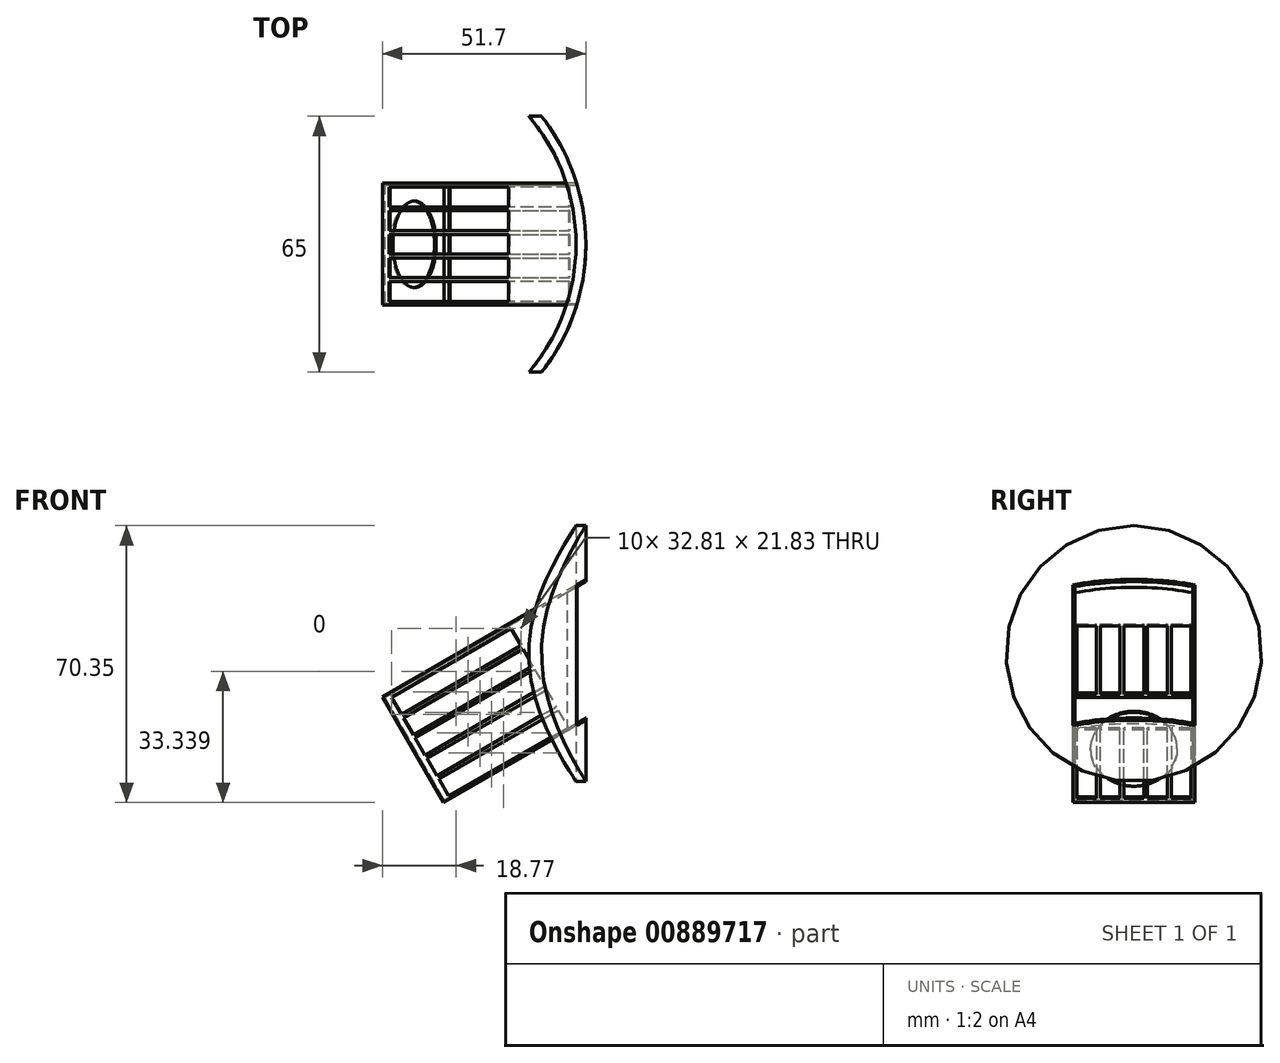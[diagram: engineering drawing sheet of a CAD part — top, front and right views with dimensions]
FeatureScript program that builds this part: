
annotation { "Feature Type Name" : "Feature", "Feature Type Description" : "" }
export const myFeature = defineFeature(function(context is Context, id is Id, definition is map)
    precondition{}
    {
        {
            var Q0;
            Q0=qCreatedBy(makeId("Top.planeOp"),FACE);
            var sketch = newSketch(context, id + "F0", { "sketchPlane" : qUnion([Q0])});
            skCircle(sketch, "E0", {"center": v(0, 0) * mm, "radius": 52.5 * mm});
            skCircle(sketch, "E1", {"center": v(0, 0) * mm, "radius": 50 * mm});
            skSolve(sketch);
        }
        {
            var Q0;
            Q0=makeQuery(id+"F0.imprint","IMPRINT",FACE,{"disambiguationData":[TD([[makeQuery(id+"F0.imprint","IMPRINT",EDGE,{"derivedFrom":sQuery(id+"F0.wireOp",EDGE,"E0")}),1.0]])]});
            var Q1;
            Q1=sQuery(id+"F0.wireOp",EDGE,"E1");
            var Q2;
            Q2=sQuery(id+"F0.wireOp",EDGE,"E0");
            extrude(context, id + "F1", {"entities" : qUnion([Q0]), "surfaceEntities" : qUnion([Q1, Q2]), "endBound" : BoundingType.SYMMETRIC, "depth" : 100 * mm, "offsetDistance" : 25 * mm});
        }
        {
            var Q0;
            Q0=qCreatedBy(makeId("Right.planeOp"),FACE);
            var sketch = newSketch(context, id + "F2", { "sketchPlane" : qUnion([Q0])});
            skCircle(sketch, "E2", {"center": v(0, 0) * mm, "radius": 32.5 * mm});
            skSolve(sketch);
        }
        {
            var Q0;
            Q0=makeQuery(id+"F2.imprint","IMPRINT",FACE,{"disambiguationData":[TD([[makeQuery(id+"F2.imprint","IMPRINT",EDGE,{"derivedFrom":sQuery(id+"F2.wireOp",EDGE,"E2")}),1.0]])]});
            var Q1;
            Q1=sQuery(id+"F2.wireOp",EDGE,"E2");
            extrude(context, id + "F3", {"entities" : qUnion([Q0]), "surfaceEntities" : qUnion([Q1]), "depth" : 60 * mm, "offsetDistance" : 25 * mm});
        }
        {
            var Q0;
            Q0=qCreatedBy(makeId("Right.planeOp"),FACE);
            var sketch = newSketch(context, id + "F4", { "sketchPlane" : qUnion([Q0])});
            skLineSegment(sketch, "E3.bottom", {"start": v(15.5, -15.5) * mm, "end": v(-15.5, -15.5) * mm});
            skLineSegment(sketch, "E3.top", {"start": v(15.5, 15.5) * mm, "end": v(-15.5, 15.5) * mm});
            skLineSegment(sketch, "E3.left", {"start": v(15.5, -15.5) * mm, "end": v(15.5, 15.5) * mm});
            skLineSegment(sketch, "E3.right", {"start": v(-15.5, -15.5) * mm, "end": v(-15.5, 15.5) * mm});
            skPoint(sketch, "E3.middle", {"position": v(0, 0) * mm});
            skSolve(sketch);
        }
        {
            var Q0;
            Q0=makeQuery(id+"F3.opExtrude","SWEPT_BODY",BODY,{"disambiguationData":[OSD([sQuery(id+"F2.wireOp",EDGE,"E2")])]});
            var Q1;
            Q1=makeQuery(id+"F1.opExtrude","SWEPT_BODY",BODY,{"disambiguationData":[OSD([sQuery(id+"F0.wireOp",EDGE,"E0"),sQuery(id+"F0.wireOp",EDGE,"E1")])]});
            booleanBodies(context, id + "F5", {"operationType" : BooleanOperationType.INTERSECTION, "tools" : qUnion([Q0, Q1])});
        }
        {
            var Q0;
            Q0 = qSketchRegion(id + "F4", true);
            extrude(context, id + "F6", {"entities" : qUnion([Q0]), "depth" : 60 * mm, "offsetDistance" : 25 * mm});
        }
        {
            var Q0;
            Q0=makeQuery(id+"F6.opExtrude","CAP_FACE",FACE,{"disambiguationData":[OSD([sQuery(id+"F4.wireOp",EDGE,"E3.bottom"),sQuery(id+"F4.wireOp",EDGE,"E3.top"),sQuery(id+"F4.wireOp",EDGE,"E3.left"),sQuery(id+"F4.wireOp",EDGE,"E3.right")])],"isStart":false});
            var sketch = newSketch(context, id + "F7", { "sketchPlane" : qUnion([Q0])});
            skLineSegment(sketch, "E4.bottom", {"start": v(-15, -15) * mm, "end": v(15, -15) * mm});
            skLineSegment(sketch, "E4.top", {"start": v(-15, 15) * mm, "end": v(15, 15) * mm});
            skLineSegment(sketch, "E4.left", {"start": v(-15, -15) * mm, "end": v(-15, 15) * mm});
            skLineSegment(sketch, "E4.right", {"start": v(15, -15) * mm, "end": v(15, 15) * mm});
            skPoint(sketch, "E4.middle", {"position": v(0, 0) * mm});
            skSolve(sketch);
        }
        {
            var Q0;
            Q0=makeQuery(id+"F7.imprint","IMPRINT",FACE,{"disambiguationData":[TD([[makeQuery(id+"F7.imprint","IMPRINT",EDGE,{"derivedFrom":sQuery(id+"F7.wireOp",EDGE,"E4.bottom")}),1.0]])]});
            extrude(context, id + "F8", {"entities" : qUnion([Q0]), "operationType" : NewBodyOperationType.REMOVE, "oppositeDirection" : true, "depth" : 59.5 * mm, "offsetDistance" : 25 * mm});
        }
        {
            var Q0;
            Q0=makeQuery(id+"F6.opExtrude","SWEPT_FACE",FACE,{"disambiguationData":[OSD([sQuery(id+"F4.wireOp",EDGE,"E3.top")])]});
            var sketch = newSketch(context, id + "F9", { "sketchPlane" : qUnion([Q0])});
            skLineSegment(sketch, "E5.bottom", {"start": v(2, -14.5) * mm, "end": v(37, -14.5) * mm});
            skLineSegment(sketch, "E5.top", {"start": v(2, -9.5) * mm, "end": v(37, -9.5) * mm});
            skLineSegment(sketch, "E5.left", {"start": v(2, -14.5) * mm, "end": v(2, -9.5) * mm});
            skLineSegment(sketch, "E6.bottom", {"start": v(37, -8.5) * mm, "end": v(2, -8.5) * mm});
            skLineSegment(sketch, "E6.top", {"start": v(37, -3.5) * mm, "end": v(2, -3.5) * mm});
            skLineSegment(sketch, "E6.left", {"start": v(37, -8.5) * mm, "end": v(37, -3.5) * mm});
            skLineSegment(sketch, "E6.right", {"start": v(2, -8.5) * mm, "end": v(2, -3.5) * mm});
            skLineSegment(sketch, "E7.bottom", {"start": v(37, -2.5) * mm, "end": v(2, -2.5) * mm});
            skLineSegment(sketch, "E7.top", {"start": v(37, 2.5) * mm, "end": v(2, 2.5) * mm});
            skLineSegment(sketch, "E7.left", {"start": v(37, -2.5) * mm, "end": v(37, 2.5) * mm});
            skLineSegment(sketch, "E7.right", {"start": v(2, -2.5) * mm, "end": v(2, 2.5) * mm});
            skLineSegment(sketch, "E8.bottom", {"start": v(37, 3.5) * mm, "end": v(2, 3.5) * mm});
            skLineSegment(sketch, "E8.top", {"start": v(37, 8.5) * mm, "end": v(2, 8.5) * mm});
            skLineSegment(sketch, "E8.left", {"start": v(37, 3.5) * mm, "end": v(37, 8.5) * mm});
            skLineSegment(sketch, "E8.right", {"start": v(2, 3.5) * mm, "end": v(2, 8.5) * mm});
            skLineSegment(sketch, "E9.bottom", {"start": v(2, 9.5) * mm, "end": v(37, 9.5) * mm});
            skLineSegment(sketch, "E9.top", {"start": v(2, 14.5) * mm, "end": v(37, 14.5) * mm});
            skLineSegment(sketch, "E9.left", {"start": v(2, 9.5) * mm, "end": v(2, 14.5) * mm});
            skLineSegment(sketch, "E9.right", {"start": v(37, 9.5) * mm, "end": v(37, 14.5) * mm});
            skLineSegment(sketch, "E10", {"start": v(37, -14.5) * mm, "end": v(37, -9.5) * mm});
            skSolve(sketch);
        }
        {
            var Q0;
            Q0=makeQuery(id+"F9.imprint","IMPRINT",FACE,{"disambiguationData":[TD([[makeQuery(id+"F9.imprint","IMPRINT",EDGE,{"derivedFrom":sQuery(id+"F9.wireOp",EDGE,"E5.bottom")}),1.0]])]});
            var Q1;
            Q1=makeQuery(id+"F9.imprint","IMPRINT",FACE,{"disambiguationData":[TD([[makeQuery(id+"F9.imprint","IMPRINT",EDGE,{"derivedFrom":sQuery(id+"F9.wireOp",EDGE,"E6.bottom")}),-1.0]])]});
            var Q2;
            Q2=makeQuery(id+"F9.imprint","IMPRINT",FACE,{"disambiguationData":[TD([[makeQuery(id+"F9.imprint","IMPRINT",EDGE,{"derivedFrom":sQuery(id+"F9.wireOp",EDGE,"E7.bottom")}),-1.0]])]});
            var Q3;
            Q3=makeQuery(id+"F9.imprint","IMPRINT",FACE,{"disambiguationData":[TD([[makeQuery(id+"F9.imprint","IMPRINT",EDGE,{"derivedFrom":sQuery(id+"F9.wireOp",EDGE,"E8.bottom")}),-1.0]])]});
            var Q4;
            Q4=makeQuery(id+"F9.imprint","IMPRINT",FACE,{"disambiguationData":[TD([[makeQuery(id+"F9.imprint","IMPRINT",EDGE,{"derivedFrom":sQuery(id+"F9.wireOp",EDGE,"E9.bottom")}),1.0]])]});
            extrude(context, id + "F10", {"entities" : qUnion([Q0, Q1, Q2, Q3, Q4]), "operationType" : NewBodyOperationType.REMOVE, "oppositeDirection" : true, "depth" : 50 * mm, "offsetDistance" : 25 * mm});
        }
        {
            var Q0;
            Q0=makeQuery(id+"F6.opExtrude","SWEPT_FACE",FACE,{"disambiguationData":[OSD([sQuery(id+"F4.wireOp",EDGE,"E3.right")])]});
            var sketch = newSketch(context, id + "F11", { "sketchPlane" : qUnion([Q0])});
            skLineSegment(sketch, "E11.bottom", {"start": v(2, 14.23) * mm, "end": v(37, 14.23) * mm});
            skLineSegment(sketch, "E11.top", {"start": v(2, 9.23) * mm, "end": v(37, 9.23) * mm});
            skLineSegment(sketch, "E11.left", {"start": v(2, 14.23) * mm, "end": v(2, 9.23) * mm});
            skLineSegment(sketch, "E11.right", {"start": v(37, 14.23) * mm, "end": v(37, 9.23) * mm});
            skLineSegment(sketch, "E12.bottom", {"start": v(2, 8.23) * mm, "end": v(37, 8.23) * mm});
            skLineSegment(sketch, "E12.top", {"start": v(2, 3.23) * mm, "end": v(37, 3.23) * mm});
            skLineSegment(sketch, "E12.left", {"start": v(2, 8.23) * mm, "end": v(2, 3.23) * mm});
            skLineSegment(sketch, "E12.right", {"start": v(37, 8.23) * mm, "end": v(37, 3.23) * mm});
            skLineSegment(sketch, "E13.bottom", {"start": v(2, 2.23) * mm, "end": v(37, 2.23) * mm});
            skLineSegment(sketch, "E13.top", {"start": v(2, -2.77) * mm, "end": v(37, -2.77) * mm});
            skLineSegment(sketch, "E13.left", {"start": v(2, 2.23) * mm, "end": v(2, -2.77) * mm});
            skLineSegment(sketch, "E13.right", {"start": v(37, 2.23) * mm, "end": v(37, -2.77) * mm});
            skLineSegment(sketch, "E14.bottom", {"start": v(2, -3.77) * mm, "end": v(37, -3.77) * mm});
            skLineSegment(sketch, "E14.top", {"start": v(2, -8.77) * mm, "end": v(37, -8.77) * mm});
            skLineSegment(sketch, "E14.left", {"start": v(2, -3.77) * mm, "end": v(2, -8.77) * mm});
            skLineSegment(sketch, "E14.right", {"start": v(37, -3.77) * mm, "end": v(37, -8.77) * mm});
            skLineSegment(sketch, "E15.bottom", {"start": v(2, -9.77) * mm, "end": v(37, -9.77) * mm});
            skLineSegment(sketch, "E15.top", {"start": v(2, -14.77) * mm, "end": v(37, -14.77) * mm});
            skLineSegment(sketch, "E15.left", {"start": v(2, -9.77) * mm, "end": v(2, -14.77) * mm});
            skLineSegment(sketch, "E15.right", {"start": v(37, -9.77) * mm, "end": v(37, -14.77) * mm});
            skSolve(sketch);
        }
        {
            var Q0;
            Q0=makeQuery(id+"F11.imprint","IMPRINT",FACE,{"disambiguationData":[TD([[makeQuery(id+"F11.imprint","IMPRINT",EDGE,{"derivedFrom":sQuery(id+"F11.wireOp",EDGE,"E11.bottom")}),-1.0]])]});
            var Q1;
            Q1=makeQuery(id+"F11.imprint","IMPRINT",FACE,{"disambiguationData":[TD([[makeQuery(id+"F11.imprint","IMPRINT",EDGE,{"derivedFrom":sQuery(id+"F11.wireOp",EDGE,"E12.bottom")}),-1.0]])]});
            var Q2;
            Q2=makeQuery(id+"F11.imprint","IMPRINT",FACE,{"disambiguationData":[TD([[makeQuery(id+"F11.imprint","IMPRINT",EDGE,{"derivedFrom":sQuery(id+"F11.wireOp",EDGE,"E13.bottom")}),-1.0]])]});
            var Q3;
            Q3=makeQuery(id+"F11.imprint","IMPRINT",FACE,{"disambiguationData":[TD([[makeQuery(id+"F11.imprint","IMPRINT",EDGE,{"derivedFrom":sQuery(id+"F11.wireOp",EDGE,"E14.bottom")}),-1.0]])]});
            var Q4;
            Q4=makeQuery(id+"F11.imprint","IMPRINT",FACE,{"disambiguationData":[TD([[makeQuery(id+"F11.imprint","IMPRINT",EDGE,{"derivedFrom":sQuery(id+"F11.wireOp",EDGE,"E15.bottom")}),-1.0]])]});
            extrude(context, id + "F12", {"entities" : qUnion([Q0, Q1, Q2, Q3, Q4]), "operationType" : NewBodyOperationType.REMOVE, "oppositeDirection" : true, "depth" : 50 * mm, "offsetDistance" : 25 * mm});
        }
        {
            var Q0;
            Q0=makeQuery(id+"F6.opExtrude","CAP_FACE",FACE,{"disambiguationData":[OSD([sQuery(id+"F4.wireOp",EDGE,"E3.bottom"),sQuery(id+"F4.wireOp",EDGE,"E3.top"),sQuery(id+"F4.wireOp",EDGE,"E3.left"),sQuery(id+"F4.wireOp",EDGE,"E3.right")])],"isStart":true});
            var sketch = newSketch(context, id + "F13", { "sketchPlane" : qUnion([Q0])});
            skCircle(sketch, "E16", {"center": v(0, 0) * mm, "radius": 11 * mm});
            skSolve(sketch);
        }
        {
            var Q0;
            Q0=makeQuery(id+"F13.imprint","IMPRINT",FACE,{"disambiguationData":[TD([[makeQuery(id+"F13.imprint","IMPRINT",EDGE,{"derivedFrom":sQuery(id+"F13.wireOp",EDGE,"E16")}),1.0]])]});
            extrude(context, id + "F14", {"entities" : qUnion([Q0]), "operationType" : NewBodyOperationType.REMOVE, "oppositeDirection" : true, "depth" : 25 * mm, "offsetDistance" : 25 * mm});
        }
        {
            var Q0;
            Q0=makeQuery(id+"F6.opExtrude","SWEPT_BODY",BODY,{"disambiguationData":[OSD([sQuery(id+"F4.wireOp",EDGE,"E3.bottom"),sQuery(id+"F4.wireOp",EDGE,"E3.top"),sQuery(id+"F4.wireOp",EDGE,"E3.left"),sQuery(id+"F4.wireOp",EDGE,"E3.right")])]});
            var Q1;
            Q1=makeQuery(id+"F6.opExtrude","CAP_EDGE",EDGE,{"disambiguationData":[OSD([sQuery(id+"F4.wireOp",EDGE,"E3.top")])],"isStart":true});
            transform(context, id + "F15", {"entities" : qUnion([Q0]), "transformType" : TransformType.ROTATION, "transformAxis" : qUnion([Q1]), "angle" : 30 * degree, "makeCopy" : false});
        }
        {
            var Q0;
            Q0=makeQuery(id+"F6.opExtrude","SWEPT_BODY",BODY,{"disambiguationData":[OSD([sQuery(id+"F4.wireOp",EDGE,"E3.bottom"),sQuery(id+"F4.wireOp",EDGE,"E3.top"),sQuery(id+"F4.wireOp",EDGE,"E3.left"),sQuery(id+"F4.wireOp",EDGE,"E3.right")])]});
            transform(context, id + "F16", {"entities" : qUnion([Q0]), "transformType" : TransformType.TRANSLATION_3D, "dx" : 0.8 * mm, "dy" : 0 * mm, "dz" : -26.5 * mm, "makeCopy" : false});
        }
        {
            var Q0;
            Q0=makeQuery(id+"F6.opExtrude","CAP_FACE",FACE,{"disambiguationData":[OSD([sQuery(id+"F4.wireOp",EDGE,"E3.bottom"),sQuery(id+"F4.wireOp",EDGE,"E3.top"),sQuery(id+"F4.wireOp",EDGE,"E3.left"),sQuery(id+"F4.wireOp",EDGE,"E3.right")])],"isStart":false});
            var sketch = newSketch(context, id + "F17", { "sketchPlane" : qUnion([Q0])});
            skLineSegment(sketch, "E17.bottom", {"start": v(-15, -10.43) * mm, "end": v(15, -10.43) * mm});
            skLineSegment(sketch, "E17.top", {"start": v(-15, -40.43) * mm, "end": v(15, -40.43) * mm});
            skLineSegment(sketch, "E17.left", {"start": v(-15, -10.43) * mm, "end": v(-15, -40.43) * mm});
            skLineSegment(sketch, "E17.right", {"start": v(15, -10.43) * mm, "end": v(15, -40.43) * mm});
            skSolve(sketch);
        }
        {
            var Q0;
            Q0 = qSketchRegion(id + "F17", true);
            extrude(context, id + "F18", {"entities" : qUnion([Q0]), "operationType" : NewBodyOperationType.REMOVE, "oppositeDirection" : true, "depth" : 25 * mm, "offsetDistance" : 25 * mm});
        }
        {
            var Q0;
            Q0=qCreatedBy(makeId("Top.planeOp"),FACE);
            var sketch = newSketch(context, id + "F19", { "sketchPlane" : qUnion([Q0])});
            skCircle(sketch, "E18", {"center": v(0, 0) * mm, "radius": 52.5 * mm});
            skSolve(sketch);
        }
        {
            var Q0;
            Q0=makeQuery(id+"F19.imprint","IMPRINT",FACE,{"disambiguationData":[TD([[makeQuery(id+"F19.imprint","IMPRINT",EDGE,{"derivedFrom":sQuery(id+"F19.wireOp",EDGE,"E18")}),1.0]])]});
            extrude(context, id + "F20", {"entities" : qUnion([Q0]), "endBound" : BoundingType.SYMMETRIC, "depth" : 100 * mm, "offsetDistance" : 25 * mm});
        }
        {
            var Q0;
            Q0=makeQuery(id+"F6.opExtrude","SWEPT_BODY",BODY,{"disambiguationData":[OSD([sQuery(id+"F4.wireOp",EDGE,"E3.bottom"),sQuery(id+"F4.wireOp",EDGE,"E3.top"),sQuery(id+"F4.wireOp",EDGE,"E3.left"),sQuery(id+"F4.wireOp",EDGE,"E3.right")])]});
            var Q1;
            Q1=makeQuery(id+"F20.opExtrude","SWEPT_BODY",BODY,{"disambiguationData":[OSD([sQuery(id+"F19.wireOp",EDGE,"E18")])]});
            booleanBodies(context, id + "F21", {"operationType" : BooleanOperationType.INTERSECTION, "tools" : qUnion([Q0, Q1])});
        }
    });
